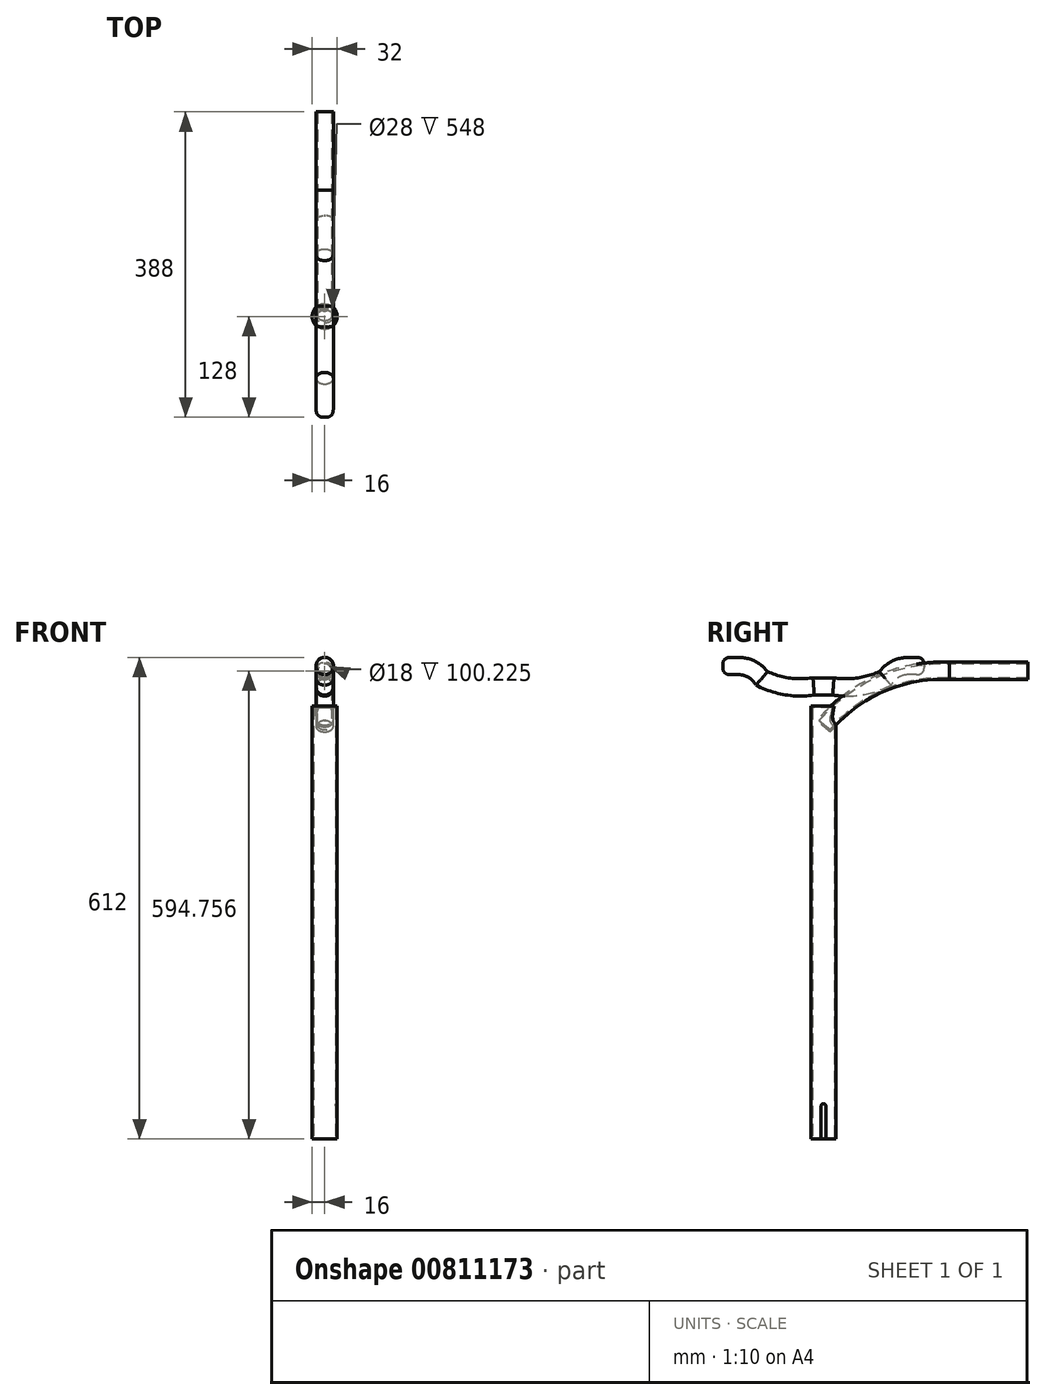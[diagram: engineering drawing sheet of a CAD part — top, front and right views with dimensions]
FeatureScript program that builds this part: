
annotation { "Feature Type Name" : "Feature", "Feature Type Description" : "" }
export const myFeature = defineFeature(function(context is Context, id is Id, definition is map)
    precondition{}
    {
        {
            var Q0;
            Q0=qCreatedBy(makeId("Top.planeOp"),FACE);
            var sketch = newSketch(context, id + "F0", { "sketchPlane" : qUnion([Q0])});
            skCircle(sketch, "E0", {"center": v(0, 0) * mm, "radius": 16 * mm});
            skSolve(sketch);
        }
        {
            var Q0;
            Q0 = qSketchRegion(id + "F0", true);
            extrude(context, id + "F1", {"entities" : qUnion([Q0]), "depth" : 550 * mm, "offsetDistance" : 25 * mm});
        }
        {
            var Q0;
            Q0=makeQuery(id+"F1.opExtrude","CAP_FACE",FACE,{"disambiguationData":[OSD([sQuery(id+"F0.wireOp",EDGE,"E0")])],"isStart":true});
            shell(context, id + "F2", {"entities" : qUnion([Q0]), "thickness" : 2 * mm});
        }
        {
            var Q0;
            Q0=qCreatedBy(makeId("Right.planeOp"),FACE);
            var sketch = newSketch(context, id + "F3", { "sketchPlane" : qUnion([Q0])});
            skLineSegment(sketch, "E1.bottom", {"start": v(3, 0) * mm, "end": v(-3, 0) * mm});
            skLineSegment(sketch, "E1.top", {"start": v(0, 45) * mm, "end": v(0, 45) * mm});
            skLineSegment(sketch, "E1.left", {"start": v(3, 0) * mm, "end": v(3, 42) * mm});
            skLineSegment(sketch, "E1.right", {"start": v(-3, 0) * mm, "end": v(-3, 42) * mm});
            skPoint(sketch, "E2.visualSharp", {"position": v(-3, 45) * mm});
            skArc(sketch, "E2.filletArc", {"start": v(0, 45) * mm, "mid": v(-2.12, 44.12) * mm, "end": v(-3, 42) * mm});
            skPoint(sketch, "E3.visualSharp", {"position": v(3, 45) * mm});
            skArc(sketch, "E3.filletArc", {"start": v(3, 42) * mm, "mid": v(2.12, 44.12) * mm, "end": v(0, 45) * mm});
            skSolve(sketch);
        }
        {
            var Q0;
            Q0 = qSketchRegion(id + "F3", true);
            extrude(context, id + "F4", {"entities" : qUnion([Q0]), "operationType" : NewBodyOperationType.REMOVE, "endBound" : BoundingType.THROUGH_ALL, "depth" : 25 * mm, "offsetDistance" : 25 * mm});
        }
        {
            var Q0;
            Q0=qCreatedBy(makeId("Right.planeOp"),FACE);
            var sketch = newSketch(context, id + "F5", { "sketchPlane" : qUnion([Q0])});
            skArc(sketch, "E4", {"start": v(160, 594.76) * mm, "mid": v(71.66, 578.47) * mm, "end": v(0, 524.3) * mm});
            skLineSegment(sketch, "E5", {"start": v(160, 594.76) * mm, "end": v(260, 594.76) * mm});
            skSolve(sketch);
        }
        {
            var Q0;
            Q0=sQuery(id+"F5.wireOp",VERTEX,"E5.end");
            var Q1;
            Q1=qCreatedBy(makeId("Front.planeOp"),FACE);
            cPlane(context, id + "F6", {"entities" : qUnion([Q0, Q1]), "cplaneType" : CPlaneType.PLANE_POINT, "offset" : 25 * mm, "width" : 150 * mm, "height" : 150 * mm});
        }
        {
            var Q0;
            Q0=qCreatedBy(id+"F6.planeOp",FACE);
            var sketch = newSketch(context, id + "F7", { "sketchPlane" : qUnion([Q0])});
            skCircle(sketch, "E6", {"center": v(0, 594.76) * mm, "radius": 11 * mm});
            skSolve(sketch);
        }
        {
            var Q0;
            Q0 = qSketchRegion(id + "F7", true);
            var Q1;
            Q1 = qConstructionFilter(qBodyType(qCreatedBy(id + "F5" ,EDGE), BodyType.WIRE), ConstructionObject.NO);
            sweep(context, id + "F8", {"operationType" : NewBodyOperationType.ADD, "profiles" : qUnion([Q0]), "path" : qUnion([Q1])});
        }
        {
            var Q0;
            Q0=makeQuery(id+"F8.opSweep","CAP_FACE",FACE,{"disambiguationData":[OSD([sQuery(id+"F5.wireOp",VERTEX,"E5.end"),sQuery(id+"F7.wireOp",EDGE,"E6")])],"isStart":true});
            shell(context, id + "F9", {"entities" : qUnion([Q0]), "thickness" : 2 * mm});
        }
        {
            var Q0;
            Q0=qCreatedBy(makeId("Right.planeOp"),FACE);
            var sketch = newSketch(context, id + "F10", { "sketchPlane" : qUnion([Q0])});
            skLineSegment(sketch, "E7", {"start": v(0, 538.46) * mm, "end": v(0, 575) * mm, "construction": true});
            skLineSegment(sketch, "E8", {"start": v(-128, 601) * mm, "end": v(-108, 601) * mm});
            skArc(sketch, "E9", {"start": v(-78.28, 585.23) * mm, "mid": v(-91.18, 596.81) * mm, "end": v(-108, 601) * mm});
            skArc(sketch, "E10", {"start": v(-78.28, 585.23) * mm, "mid": v(-46.17, 575.11) * mm, "end": v(-12.5, 575) * mm});
            skLineSegment(sketch, "E11", {"start": v(-12.5, 575) * mm, "end": v(0, 575) * mm});
            skArc(sketch, "E12.MirrorCS", {"start": v(78.28, 585.23) * mm, "mid": v(46.17, 575.11) * mm, "end": v(12.5, 575) * mm});
            skLineSegment(sketch, "E13.MirrorCS", {"start": v(12.5, 575) * mm, "end": v(0, 575) * mm});
            skArc(sketch, "E14.MirrorCS", {"start": v(78.28, 585.23) * mm, "mid": v(91.18, 596.81) * mm, "end": v(108, 601) * mm});
            skLineSegment(sketch, "E15.MirrorCS", {"start": v(128, 601) * mm, "end": v(108, 601) * mm});
            skSolve(sketch);
        }
        {
            var Q0;
            Q0=sQuery(id+"F10.wireOp",VERTEX,"E15.MirrorCS.start");
            var Q1;
            Q1=qCreatedBy(id+"F6.planeOp",FACE);
            cPlane(context, id + "F11", {"entities" : qUnion([Q0, Q1]), "cplaneType" : CPlaneType.PLANE_POINT, "offset" : 25 * mm, "width" : 150 * mm, "height" : 150 * mm});
        }
        {
            var Q0;
            Q0=qCreatedBy(id+"F11.planeOp",FACE);
            var sketch = newSketch(context, id + "F12", { "sketchPlane" : qUnion([Q0])});
            skCircle(sketch, "E16", {"center": v(0, 601) * mm, "radius": 11 * mm});
            skSolve(sketch);
        }
        {
            var Q0;
            Q0 = qSketchRegion(id + "F12", true);
            var Q1;
            Q1 = qConstructionFilter(qBodyType(qCreatedBy(id + "F10" ,EDGE), BodyType.WIRE), ConstructionObject.NO);
            sweep(context, id + "F13", {"profiles" : qUnion([Q0]), "path" : qUnion([Q1])});
        }
        {
            var Q0;
            Q0=makeQuery(id+"F13.opSweep","CAP_EDGE",EDGE,{"disambiguationData":[OSD([sQuery(id+"F10.wireOp",VERTEX,"E15.MirrorCS.start"),sQuery(id+"F12.wireOp",EDGE,"E16")])],"isStart":true});
            var Q1;
            Q1=makeQuery(id+"F13.opSweep","CAP_EDGE",EDGE,{"disambiguationData":[OSD([sQuery(id+"F10.wireOp",VERTEX,"E8.start"),sQuery(id+"F12.wireOp",EDGE,"E16")])],"isStart":false});
            fillet(context, id + "F14", {"entities" : qUnion([Q0, Q1]), "radius" : 10 * mm, "tangentPropagation" : true, "rho" : 0.5, "crossSection" : FilletCrossSection.CONIC, "allowEdgeOverflow" : false});
        }
    });
